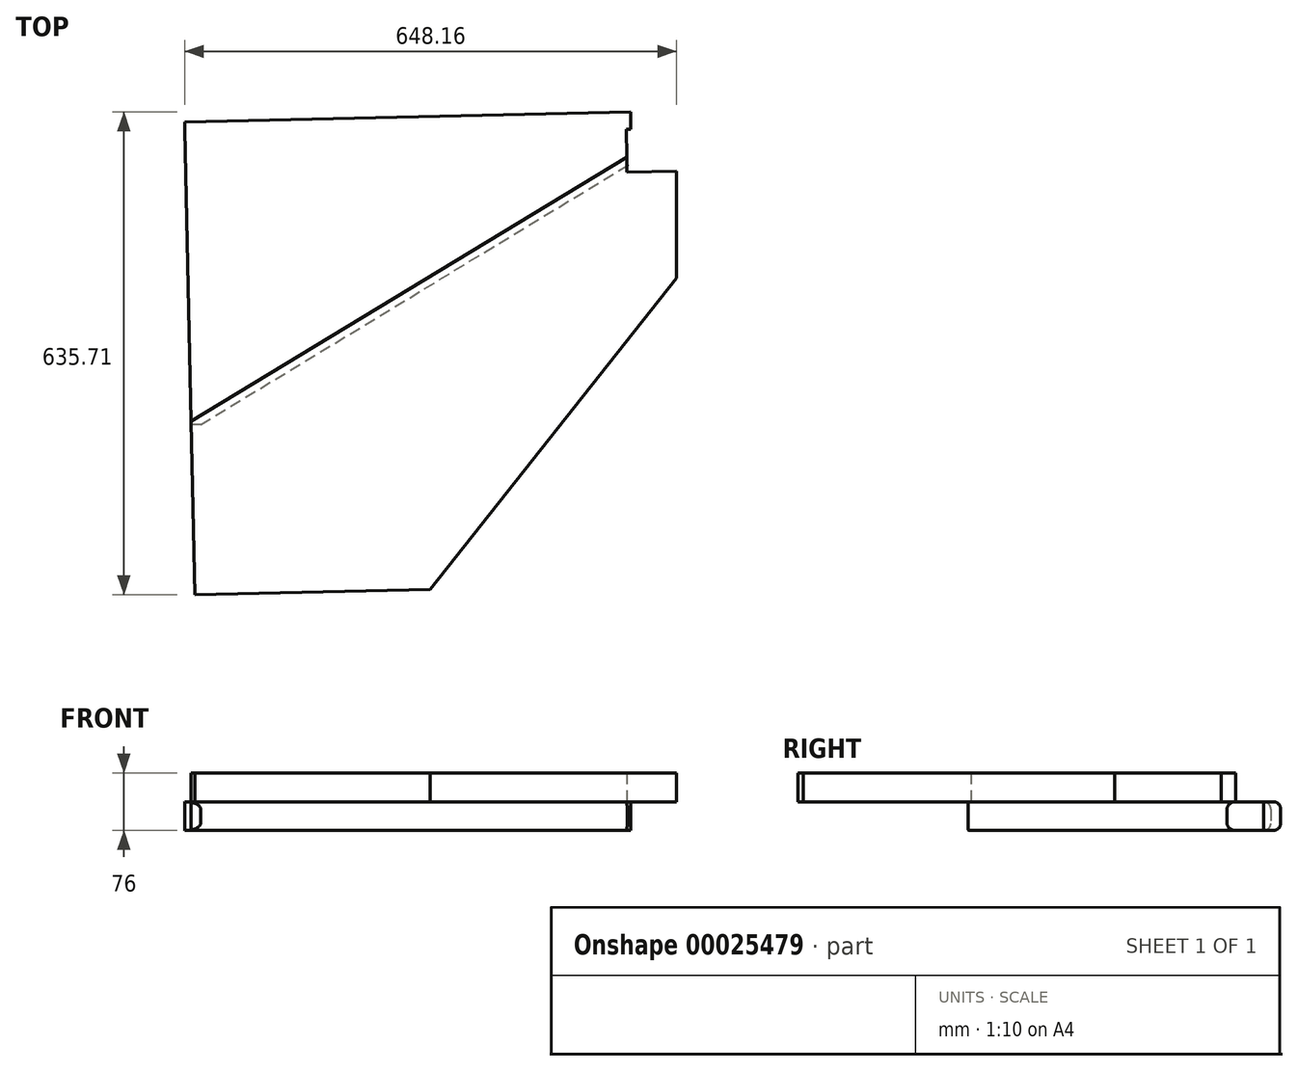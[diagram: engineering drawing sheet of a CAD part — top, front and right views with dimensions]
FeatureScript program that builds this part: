
annotation { "Feature Type Name" : "Feature", "Feature Type Description" : "" }
export const myFeature = defineFeature(function(context is Context, id is Id, definition is map)
    precondition{}
    {
        {
            var Q0;
            Q0=qCreatedBy(makeId("Top.planeOp"),FACE);
            var sketch = newSketch(context, id + "F0", { "sketchPlane" : qUnion([Q0])});
            skLineSegment(sketch, "E0.rect.bottom", {"start": v(289.3, 206) * mm, "end": v(-298.06, 193.1) * mm});
            skLineSegment(sketch, "E0.rect.right", {"start": v(-298.06, 193.1) * mm, "end": v(-289.3, -206) * mm});
            skPoint(sketch, "E0.rect.middle", {"position": v(0, 0) * mm});
            skLineSegment(sketch, "E1", {"start": v(-289.3, -206) * mm, "end": v(-276.8, -205.73) * mm});
            skLineSegment(sketch, "E2", {"start": v(-276.8, -205.73) * mm, "end": v(284.85, 135.27) * mm});
            skLineSegment(sketch, "E3", {"start": v(283.79, 183.65) * mm, "end": v(289.79, 183.75) * mm});
            skLineSegment(sketch, "E4", {"start": v(289.79, 183.75) * mm, "end": v(289.3, 206) * mm});
            skLineSegment(sketch, "E5", {"start": v(283.79, 183.65) * mm, "end": v(284.85, 135.27) * mm});
            skSolve(sketch);
        }
        {
            var Q0;
            Q0=makeQuery(id+"F0.imprint","IMPRINT",FACE,{"disambiguationData":[TD([[makeQuery(id+"F0.imprint","IMPRINT",EDGE,{"derivedFrom":sQuery(id+"F0.wireOp",EDGE,"E0.rect.bottom")}),1.0]])]});
            extrude(context, id + "F1", {"entities" : qUnion([Q0]), "depth" : 38 * mm});
        }
        {
            var Q0;
            Q0=makeQuery(id+"F1.opExtrude","CAP_EDGE",EDGE,{"disambiguationData":[OSD([sQuery(id+"F0.wireOp",EDGE,"E0.rect.bottom")])],"isStart":false});
            var Q1;
            Q1=makeQuery(id+"F1.opExtrude","CAP_EDGE",EDGE,{"disambiguationData":[OSD([sQuery(id+"F0.wireOp",EDGE,"293b06e7-427b-4fe9-8f0e-36a276c6547d")])],"isStart":false});
            var Q2;
            Q2=makeQuery(id+"F1.opExtrude","CAP_EDGE",EDGE,{"disambiguationData":[OSD([sQuery(id+"F0.wireOp",EDGE,"293b06e7-427b-4fe9-8f0e-36a276c6547d")])],"isStart":true});
            var Q3;
            Q3=makeQuery(id+"F1.opExtrude","CAP_EDGE",EDGE,{"disambiguationData":[OSD([sQuery(id+"F0.wireOp",EDGE,"E0.rect.bottom")])],"isStart":true});
            fillet(context, id + "F2", {"entities" : qUnion([Q0, Q1, Q2, Q3]), "radius" : 10 * mm, "tangentPropagation" : true, "allowEdgeOverflow" : false});
        }
        {
            var Q0;
            Q0=makeQuery(id+"F1.opExtrude","CAP_EDGE",EDGE,{"disambiguationData":[OSD([sQuery(id+"F0.wireOp",EDGE,"E2")])],"isStart":false});
            var Q1;
            Q1=makeQuery(id+"F1.opExtrude","CAP_EDGE",EDGE,{"disambiguationData":[OSD([sQuery(id+"F0.wireOp",EDGE,"E2")])],"isStart":true});
            fillet(context, id + "F3", {"entities" : qUnion([Q0, Q1]), "radius" : 10 * mm, "tangentPropagation" : true, "allowEdgeOverflow" : false});
        }
        {
            var Q0;
            Q0=makeQuery(id+"F1.opExtrude","CAP_FACE",FACE,{"disambiguationData":[OSD([sQuery(id+"F0.wireOp",EDGE,"E0.rect.bottom"),sQuery(id+"F0.wireOp",EDGE,"E0.rect.right"),sQuery(id+"F0.wireOp",EDGE,"E1"),sQuery(id+"F0.wireOp",EDGE,"E2"),sQuery(id+"F0.wireOp",EDGE,"E3"),sQuery(id+"F0.wireOp",EDGE,"E4"),sQuery(id+"F0.wireOp",EDGE,"E5")])],"isStart":false});
            var sketch = newSketch(context, id + "F4", { "sketchPlane" : qUnion([Q0])});
            skLineSegment(sketch, "E6", {"start": v(-289.8, -183.26) * mm, "end": v(284.2, 165.23) * mm});
            skLineSegment(sketch, "E7", {"start": v(-289.8, -183.26) * mm, "end": v(-284.39, -429.7) * mm});
            skLineSegment(sketch, "E8", {"start": v(-284.39, -429.7) * mm, "end": v(25.41, -422.9) * mm});
            skLineSegment(sketch, "E9", {"start": v(25.41, -422.9) * mm, "end": v(350.1, -12.5) * mm});
            skLineSegment(sketch, "E10", {"start": v(284.2, 165.23) * mm, "end": v(284.6, 127.21) * mm});
            skLineSegment(sketch, "E11", {"start": v(284.6, 127.21) * mm, "end": v(350.1, 127.91) * mm});
            skLineSegment(sketch, "E12", {"start": v(350.1, 127.91) * mm, "end": v(350.1, -12.5) * mm});
            skSolve(sketch);
        }
        {
            var Q0;
            {var subQ7=sQuery(id+"F4.wireOp",EDGE,"E8");Q0=makeQuery(id+"F4.imprint","IMPRINT",FACE,{"disambiguationData":[TD([[makeQuery(id+"F4.imprint","IMPRINT",EDGE,{"derivedFrom":subQ7}),1.0]])]});}
            extrude(context, id + "F5", {"entities" : qUnion([Q0]), "depth" : 38 * mm});
        }
    });
